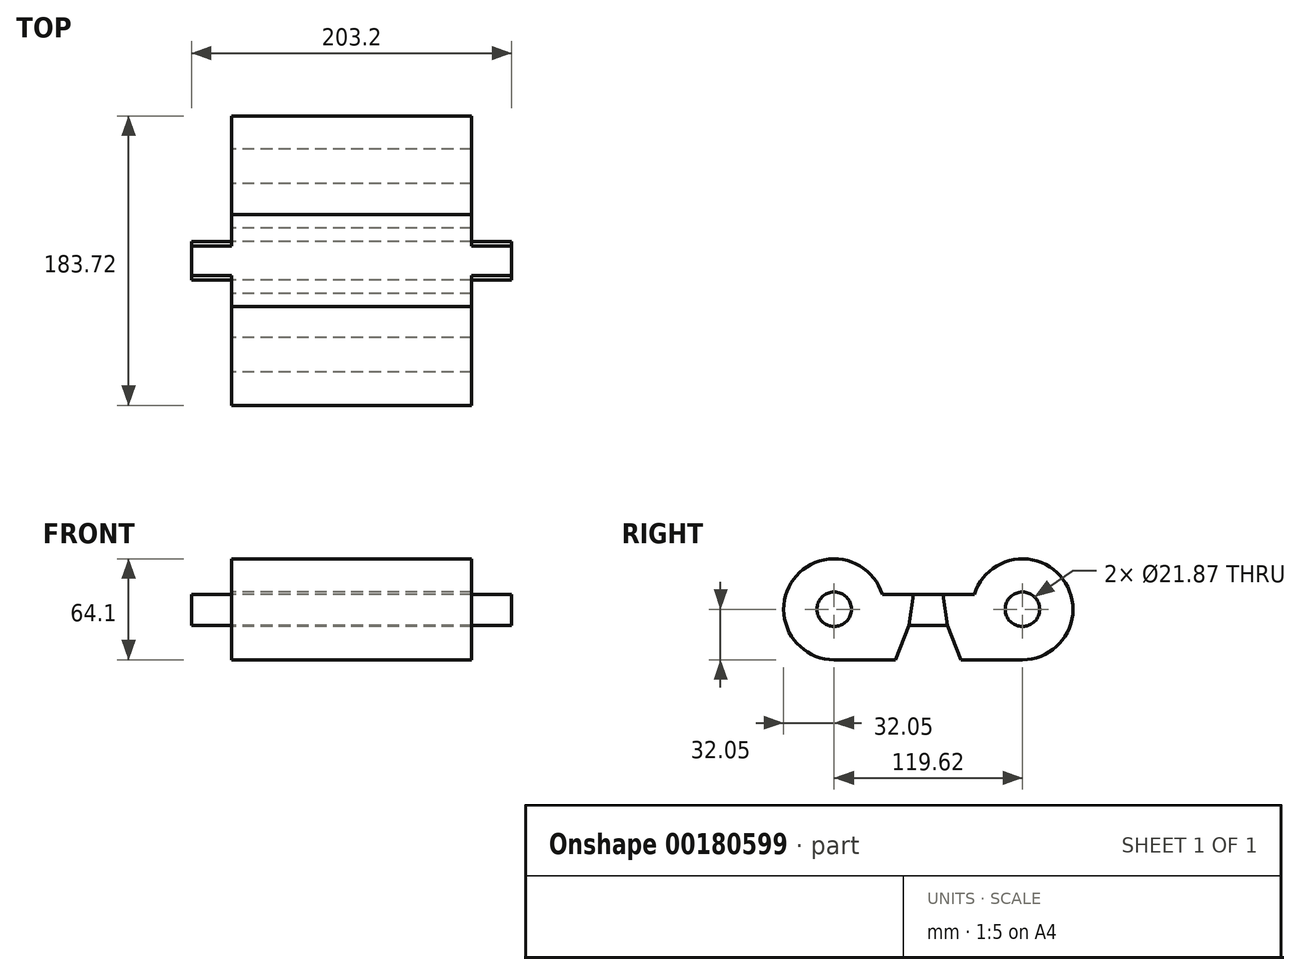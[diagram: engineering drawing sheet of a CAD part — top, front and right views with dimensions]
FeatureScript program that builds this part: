
annotation { "Feature Type Name" : "Feature", "Feature Type Description" : "" }
export const myFeature = defineFeature(function(context is Context, id is Id, definition is map)
    precondition{}
    {
        {
            var Q0;
            Q0=qCreatedBy(makeId("Right.planeOp"),FACE);
            var sketch = newSketch(context, id + "F0", { "sketchPlane" : qUnion([Q0])});
            skCircle(sketch, "E0", {"center": v(-59.8, 0) * mm, "radius": 10.94 * mm});
            skCircle(sketch, "E1", {"center": v(59.8, 0) * mm, "radius": 10.94 * mm});
            skLineSegment(sketch, "E2", {"start": v(-59.8, -32.05) * mm, "end": v(59.8, -32.05) * mm});
            skArc(sketch, "E3", {"start": v(-59.8, -32.05) * mm, "mid": v(-85.6, 19.03) * mm, "end": v(-29.18, 9.45) * mm});
            skArc(sketch, "E4", {"start": v(59.8, -32.05) * mm, "mid": v(85.6, 19.03) * mm, "end": v(29.18, 9.45) * mm});
            skLineSegment(sketch, "E5.bottom", {"start": v(-20.8, -32.05) * mm, "end": v(20.8, -32.05) * mm});
            skLineSegment(sketch, "E5.top", {"start": v(-12.31, -10.18) * mm, "end": v(12.31, -10.18) * mm});
            skLineSegment(sketch, "E5.left", {"start": v(-20.8, -32.05) * mm, "end": v(-12.31, -10.18) * mm});
            skLineSegment(sketch, "E5.right", {"start": v(20.8, -32.05) * mm, "end": v(12.31, -10.18) * mm});
            skLineSegment(sketch, "E6", {"start": v(-12.31, -10.18) * mm, "end": v(-9.44, 9.45) * mm});
            skLineSegment(sketch, "E7", {"start": v(12.31, -10.18) * mm, "end": v(9.44, 9.45) * mm});
            skPoint(sketch, "E8", {"position": v(0, 9.45) * mm});
            skPoint(sketch, "E9", {"position": v(0, -32.05) * mm});
            skLineSegment(sketch, "E10", {"start": v(-29.18, 9.45) * mm, "end": v(-9.44, 9.45) * mm});
            skLineSegment(sketch, "E11", {"start": v(9.44, 9.45) * mm, "end": v(-9.44, 9.45) * mm});
            skLineSegment(sketch, "E12", {"start": v(29.18, 9.45) * mm, "end": v(9.44, 9.45) * mm});
            skPoint(sketch, "E13", {"position": v(0, -10.18) * mm});
            skSolve(sketch);
        }
        {
            var Q0;
            Q0=makeQuery(id+"F0.imprint","IMPRINT",FACE,{"disambiguationData":[TD([[makeQuery(id+"F0.imprint","IMPRINT",EDGE,{"derivedFrom":sQuery(id+"F0.wireOp",EDGE,"E5.bottom")}),1.0]])]});
            var Q1;
            Q1=makeQuery(id+"F0.imprint","IMPRINT",FACE,{"disambiguationData":[TD([[makeQuery(id+"F0.imprint","IMPRINT",EDGE,{"derivedFrom":sQuery(id+"F0.wireOp",EDGE,"E0")}),-1.0]])]});
            var Q2;
            Q2=makeQuery(id+"F0.imprint","IMPRINT",FACE,{"disambiguationData":[TD([[makeQuery(id+"F0.imprint","IMPRINT",EDGE,{"derivedFrom":sQuery(id+"F0.wireOp",EDGE,"E5.top")}),1.0]])]});
            var Q3;
            Q3=makeQuery(id+"F0.imprint","IMPRINT",FACE,{"disambiguationData":[TD([[makeQuery(id+"F0.imprint","IMPRINT",EDGE,{"derivedFrom":sQuery(id+"F0.wireOp",EDGE,"E1")}),-1.0]])]});
            extrude(context, id + "F1", {"entities" : qUnion([Q0, Q1, Q2, Q3]), "endBound" : BoundingType.SYMMETRIC, "depth" : 152.4 * mm});
        }
        {
            var Q0;
            Q0=makeQuery(id+"F0.imprint","IMPRINT",FACE,{"disambiguationData":[TD([[makeQuery(id+"F0.imprint","IMPRINT",EDGE,{"derivedFrom":sQuery(id+"F0.wireOp",EDGE,"E5.bottom")}),1.0]])]});
            var Q1;
            Q1=makeQuery(id+"F0.imprint","IMPRINT",FACE,{"disambiguationData":[TD([[makeQuery(id+"F0.imprint","IMPRINT",EDGE,{"derivedFrom":sQuery(id+"F0.wireOp",EDGE,"E5.top")}),1.0]])]});
            extrude(context, id + "F2", {"entities" : qUnion([Q0, Q1]), "operationType" : NewBodyOperationType.ADD, "endBound" : BoundingType.SYMMETRIC, "depth" : 203.2 * mm});
        }
    });
